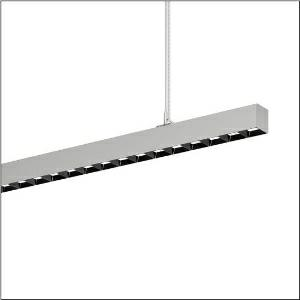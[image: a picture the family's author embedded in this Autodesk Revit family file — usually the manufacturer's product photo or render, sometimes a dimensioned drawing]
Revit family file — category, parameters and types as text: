
# Revit family: silica_21_51mx32dc3dsb
name_source: partatom
category: Lighting Fixtures
units: mm (PartAtom-declared; Revit-internal decimal feet)

## family parameters
Cut with Voids When Loaded = No
Host = Face
Light Source = No
Part Type = Normal
Room Calculation Point = No
Round Connector Dimension = Use Diameter
Shared = No

## types (1)
- --- (1 x LED, 18220 lm, 113 W, 3000K)
    Apparent Load = 113 VA
    CIE Flux Codes = 86 99 100 59 100
    Color Rendering = 80
    Color Temperature = 3000K
    Default Elevation = 1800 mm
    Description = Silica 21, office luminaire, primary light control with darklight reflector, of PMMA, black, CAT 2 (L<= 3000cd/m²), light emission: direct/indirect distribution, primary light characteristic: symmetric, installation type: suspended mounting, LED, rated luminous flux: 18.220lm, luminous efficacy: 161lm/W, light colour: 830, colour temperature: 3000K, control gear: DALI 2, with terminal, 3+2-pole, max. 2.5mm², mains connection: 220..240V, AC, 50/60Hz, rated input power: 113W, luminaire housing, of aluminium, metallic grey (RAL 9006), length: 3.004mm, width: 53mm, height: 53mm, protection rating (complete): IP20, insulation class (complete): insulation class I (protective earthing), certification: CE, permissible operating ambient temperature: 0..+35°C, standard: EN 50419, packaging unit: 1 piece
    Height = 53 mm
    Lamp = 1 x LED
    Lamp Light Flux = 18220 lm
    Lamp Power = 113 W
    Lamp count = 1
    Length = 3004 mm
    Luminous efficacy = 161 lm/W
    Manufacturer = Siteco
    ModVariant = No
    Model = 51MX32DC3DSB
    Mounting Place = Ceiling
    Mounting Type = Pendant
    Number of Poles = 1
    OnlyDefault = Yes
    Power Factor = 1
    Product Name = Silica 21
    Product group = office luminaire | ceiling pendant
    ProductGroupID = 903
    Protection Class = Protection class I
    Protection Degree = IP 20
    RLX_Detail_Level = 1
    RLX_Emergency_Light_Flux = 0 lm
    RLX_Emergency_Type = 0
    RLX_Emergency_Type_DB = No
    RlxData = <blob elided: 64437 chars, md5=06a71eb6>
    Socket = socket
    Standby Power = 0 W
    System Light Flux = 18220 lm
    System Power = 113 W
    Type Comments = factory setting: luminous flux: 100 % | dim-lin: 254 | 391 mA
    Type Image = l_1335859.jpg
    URL = http://relux.com
    VarID = @adj_122109
    Voltage = 0 V
    Weight = 0.00 kg
    Width = 53 mm

## geometry (parser evidence)
native form markers: Blend x4, Sweep x11
no freeform markers — native parametric forms only
